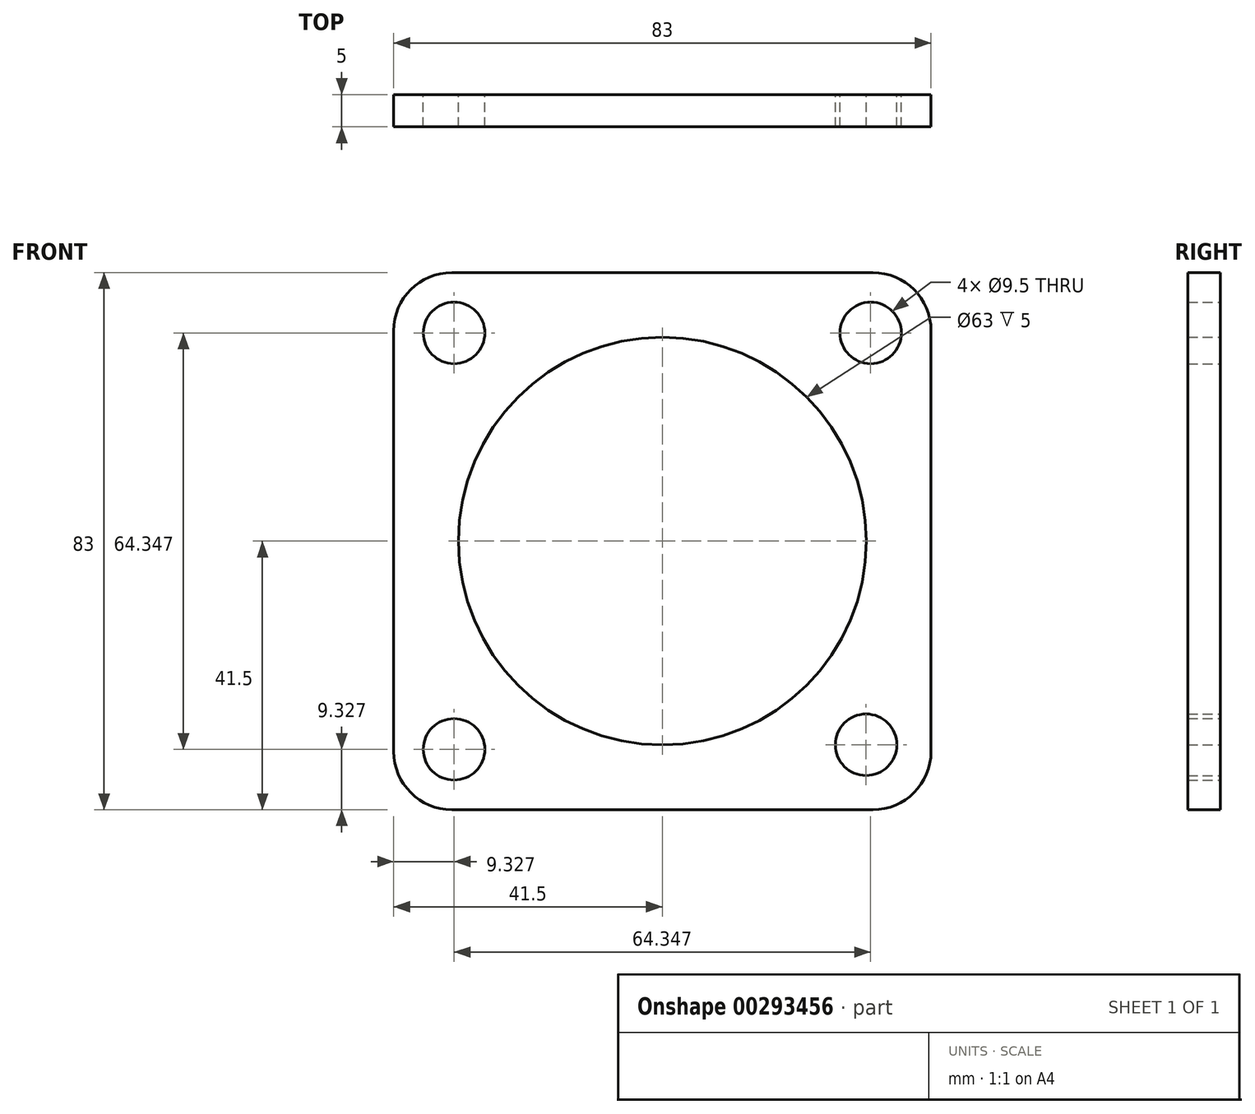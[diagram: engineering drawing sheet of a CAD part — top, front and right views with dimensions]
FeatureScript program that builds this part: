
annotation { "Feature Type Name" : "Feature", "Feature Type Description" : "" }
export const myFeature = defineFeature(function(context is Context, id is Id, definition is map)
    precondition{}
    {
        {
            var Q0;
            Q0=qCreatedBy(makeId("Front.planeOp"),FACE);
            var sketch = newSketch(context, id + "F0", { "sketchPlane" : qUnion([Q0])});
            skCircle(sketch, "E0", {"center": v(0, 0) * mm, "radius": 31.5 * mm});
            skLineSegment(sketch, "E1.bottom", {"start": v(-41.5, 41.5) * mm, "end": v(41.5, 41.5) * mm});
            skLineSegment(sketch, "E1.top", {"start": v(-41.5, -41.5) * mm, "end": v(41.5, -41.5) * mm});
            skLineSegment(sketch, "E1.left", {"start": v(-41.5, 41.5) * mm, "end": v(-41.5, -41.5) * mm});
            skLineSegment(sketch, "E1.right", {"start": v(41.5, 41.5) * mm, "end": v(41.5, -41.5) * mm});
            skLineSegment(sketch, "E2", {"start": v(-41.5, 41.5) * mm, "end": v(41.5, -41.5) * mm, "construction": true});
            skLineSegment(sketch, "E3", {"start": v(41.5, 41.5) * mm, "end": v(-41.5, -41.5) * mm, "construction": true});
            skCircle(sketch, "E4", {"center": v(-32.17, 32.17) * mm, "radius": 4.75 * mm});
            skCircle(sketch, "E5", {"center": v(32.17, 32.17) * mm, "radius": 4.75 * mm});
            skCircle(sketch, "E6", {"center": v(31.47, -31.47) * mm, "radius": 4.75 * mm});
            skCircle(sketch, "E7", {"center": v(-32.17, -32.17) * mm, "radius": 4.75 * mm});
            skCircle(sketch, "E8", {"center": v(0, 0) * mm, "radius": 45.5 * mm, "construction": true});
            skSolve(sketch);
        }
        {
            var Q0;
            Q0=makeQuery(id+"F0.imprint","IMPRINT",FACE,{"disambiguationData":[TD([[makeQuery(id+"F0.imprint","IMPRINT",EDGE,{"derivedFrom":sQuery(id+"F0.wireOp",EDGE,"E0")}),-1.0]])]});
            extrude(context, id + "F1", {"entities" : qUnion([Q0]), "depth" : 5 * mm, "offsetDistance" : 25 * mm});
        }
        {
            var Q0;
            Q0=makeQuery(id+"F1.opExtrude","SWEPT_EDGE",EDGE,{"disambiguationData":[OSD([sQuery(id+"F0.wireOp",EDGE,"E1.top"),sQuery(id+"F0.wireOp",EDGE,"E1.right")])]});
            var Q1;
            Q1=makeQuery(id+"F1.opExtrude","SWEPT_EDGE",EDGE,{"disambiguationData":[OSD([sQuery(id+"F0.wireOp",EDGE,"E1.top"),sQuery(id+"F0.wireOp",EDGE,"E1.left")])]});
            var Q2;
            Q2=makeQuery(id+"F1.opExtrude","SWEPT_EDGE",EDGE,{"disambiguationData":[OSD([sQuery(id+"F0.wireOp",EDGE,"E1.bottom"),sQuery(id+"F0.wireOp",EDGE,"E1.right")])]});
            var Q3;
            Q3=makeQuery(id+"F1.opExtrude","SWEPT_EDGE",EDGE,{"disambiguationData":[OSD([sQuery(id+"F0.wireOp",EDGE,"E1.bottom"),sQuery(id+"F0.wireOp",EDGE,"E1.left")])]});
            fillet(context, id + "F2", {"entities" : qUnion([Q0, Q1, Q2, Q3]), "tangentPropagation" : true, "radius" : 9 * mm, "defaultsChanged" : false, "vertexSettings" : [], "allowEdgeOverflow" : false});
        }
    });
